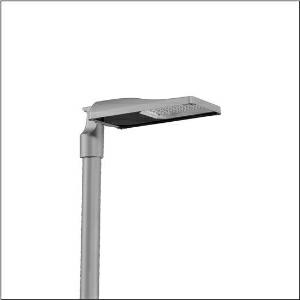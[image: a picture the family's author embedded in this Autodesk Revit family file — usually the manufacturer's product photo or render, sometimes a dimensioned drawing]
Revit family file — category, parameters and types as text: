
# Revit family: streetlight_sl_31_mini___st1_0a_5xh6d31b08ha_b8a3
name_source: partatom
category: Lighting Fixtures
units: mm (PartAtom-declared; Revit-internal decimal feet)

## family parameters
Cut with Voids When Loaded = No
Host = Face
Light Source = No
Part Type = Normal
Room Calculation Point = No
Round Connector Dimension = Use Diameter
Shared = No

## types (1)
- --- (1 x LED, 9240 lm, 68.3 W, 3000K)
    Apparent Load = 68 VA
    CIE Flux Codes = 37 72 97 100 100
    Color Rendering = 70
    Color Temperature = 3000K
    Default Elevation = 1800 mm
    Description = Streetlight SL 31 mini Easy, LST, Desk-Remote mast luminaire for post-top, side-entry; light control with lens of PMMA; light distribution: ST1.0a, direct asymmetric distribution, for standard-compliant lighting for roads and squares; LED: luminous flux: 9.240lm, light colour: 730, colour temperature: 3000K; luminous efficacy: 135,3lm/W; control: pre-setting: linear dimming characteristic, flexible luminous flux parameterisation, time-dependent luminous flux control, constant luminous flux control, power reduction, intelligent temperature release in ECG and LED module, overheat protection; luminaire housing, of diecast aluminium, SITECO metallic grey (DB 702S), corrosivity category C5 high according to DIN EN ISO 12944; cover of toughened safety glass, transparent, opened without tools; mast flange of diecast aluminium, SITECO metallic grey (DB 702S), spigot size: 76/60mm, mast flange included unmounted; with cable H07RN-F 5x 1.5mm², cable length: 8,5m, connection cable pre-assembled; mains connection: 220..240V, AC, 50/60Hz; power consumption (at start of service life): 68,3W / (at end of service life): 74,8W / (with reduced operation 50%): 29,7W; protection rating (complete): IP66; insulation class (complete): insulation class II (safety insulation); impact resistance: IK10; certification: CE, ENEC, ENEC+, VDE, UKCA; permissible operating ambient temperature for outdoor applications: -40..+50°C; packaging unit: 1 piece

Light Distribution: ST1.0a
    Height = 76 mm
    Lamp = 1 x LED
    Lamp Light Flux = 9240 lm
    Lamp Power = 68.3 W
    Lamp count = 1
    Length = 547 mm
    Luminous efficacy = 135 lm/W
    Manufacturer = Siteco
    ModVariant = No
    Model = 5XH6D31B08HA
    Number of Poles = 1
    OnlyDefault = Yes
    Power Factor = 1
    Product Name = Streetlight SL 31 mini | ST1.0a
    Product group = mast luminaire | pylon top
    ProductGroupID = 6100
    Protection Class = Protection class II
    Protection Degree = IP 66
    RLX_Detail_Level = 1
    RLX_Emergency_Light_Flux = 0 lm
    RLX_Emergency_Type = 0
    RLX_Emergency_Type_DB = No
    RlxData = <blob elided: 39569 chars, md5=c3d702c7>
    Socket = socket
    Standby Power = 0 W
    System Light Flux = 9240 lm
    System Power = 68 W
    Type Comments = factory setting: luminous flux: 100 % | dim-lin: 254 | 693 mA
    Type Image = l_1300326.jpg
    URL = http://relux.com
    VarID = @adj_060863
    Voltage = 0 V
    Weight = 0.00 kg
    Width = 265 mm

## geometry (parser evidence)
native form markers: Blend x4, Sweep x10
no freeform markers — native parametric forms only
